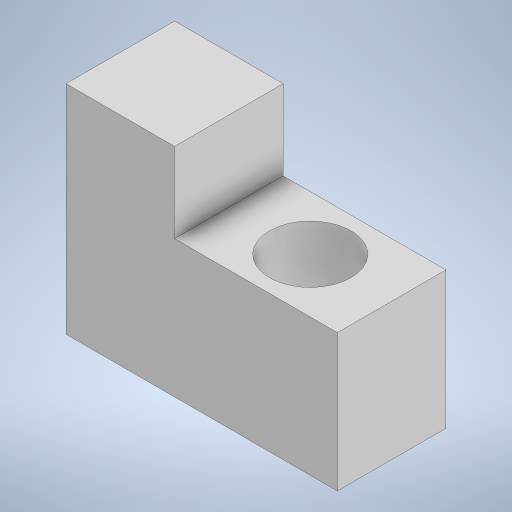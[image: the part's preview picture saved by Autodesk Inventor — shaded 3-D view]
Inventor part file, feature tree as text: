
AUTODESK INVENTOR PART (.ipt)
format: ipt  version: 2023 (Build 270158000, 158)  size: 220,672 bytes
history: native  units: in
note: dims shown in document units (in); Inventor stores cm internally (conversion verified against a paired STEP export)
features: extrude x2, sketch x1, mirror x1
ambient origin geometry x8: Origin, YZ Plane, XZ Plane, XY Plane, X Axis, Y Axis, Z Axis, Center Point
bodies: Solid1 (feature_tree)
feature tree (4):
  sketch  "Sketch1"  dims[d0=3.0in d1=2.0in d2=2.0in d3=1.5in d11=2.528in d12=0.0in d13=4.0in d14=0.0in]
  extrude  "Extrusion3"  Depth=2.0in
  extrude  "Extrusion4"  Depth=2.0in
  mirror  "Mirror1"
